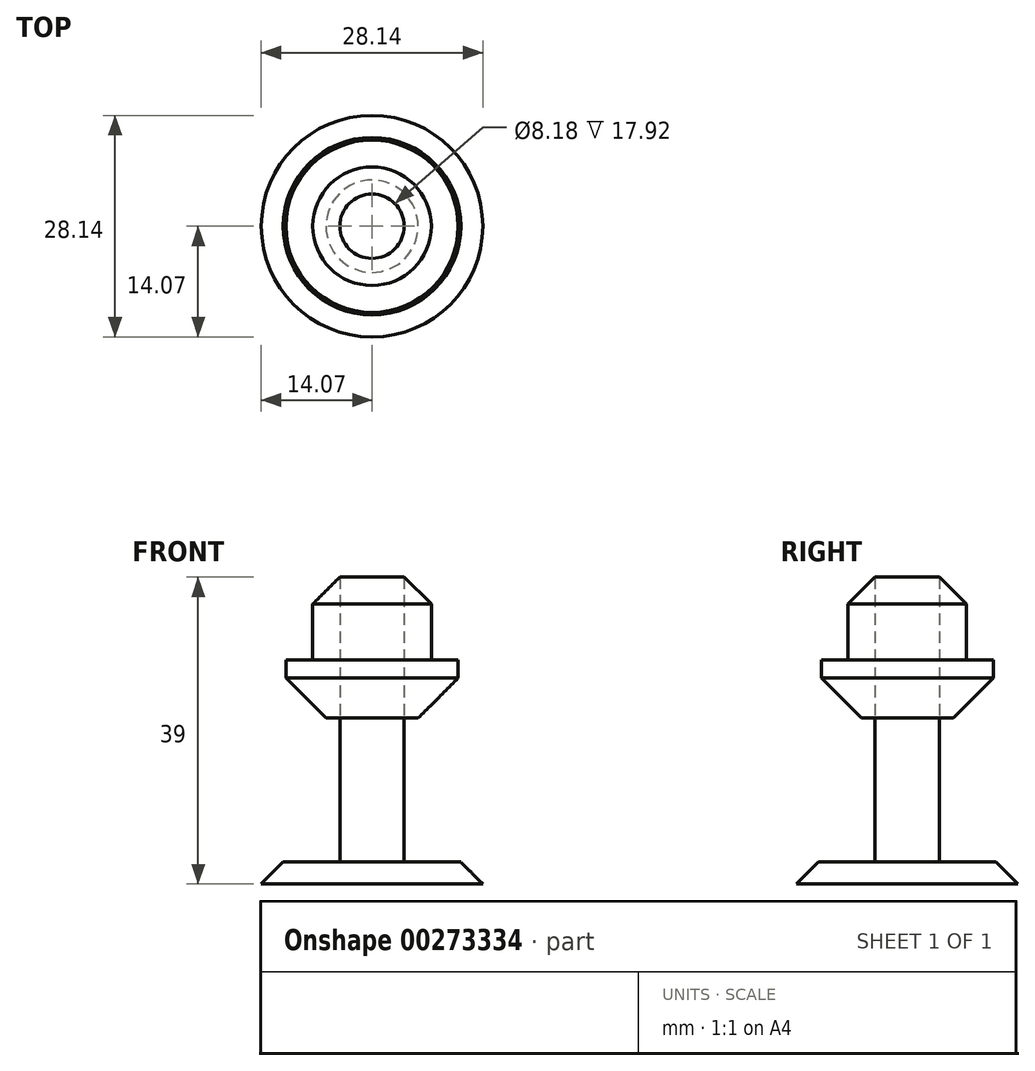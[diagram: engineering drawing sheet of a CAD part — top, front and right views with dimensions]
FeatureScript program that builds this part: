
annotation { "Feature Type Name" : "Feature", "Feature Type Description" : "" }
export const myFeature = defineFeature(function(context is Context, id is Id, definition is map)
    precondition{}
    {
        {
            var Q0;
            Q0=qCreatedBy(makeId("Top.planeOp"),FACE);
            var sketch = newSketch(context, id + "F0", { "sketchPlane" : qUnion([Q0])});
            skCircle(sketch, "E0", {"center": v(0, 0) * mm, "radius": 16.35 * mm});
            skSolve(sketch);
        }
        {
            var Q0;
            Q0=makeQuery(id+"F0.imprint","IMPRINT",FACE,{"disambiguationData":[TD([[makeQuery(id+"F0.imprint","IMPRINT",EDGE,{"derivedFrom":sQuery(id+"F0.wireOp",EDGE,"E0")}),1.0]])]});
            extrude(context, id + "F1", {"entities" : qUnion([Q0]), "depth" : 2.8 * mm});
        }
        {
            var Q0;
            Q0=makeQuery(id+"F1.opExtrude","CAP_EDGE",EDGE,{"disambiguationData":[OSD([sQuery(id+"F0.wireOp",EDGE,"E0")])],"isStart":false});
            chamfer(context, id + "F2", {"entities" : qUnion([Q0]), "width" : 5.08 * mm, "tangentPropagation" : true});
        }
        {
            var Q0;
            Q0=makeQuery(id+"F1.opExtrude","CAP_FACE",FACE,{"disambiguationData":[OSD([sQuery(id+"F0.wireOp",EDGE,"E0")])],"isStart":false});
            var sketch = newSketch(context, id + "F3", { "sketchPlane" : qUnion([Q0])});
            skCircle(sketch, "E1", {"center": v(0, 0) * mm, "radius": 5.59 * mm});
            skSolve(sketch);
        }
        {
            var Q0;
            Q0=sQuery(id+"F3.wireOp",EDGE,"E1");
            extrude(context, id + "F4", {"bodyType" : ToolBodyType.SURFACE, "surfaceEntities" : qUnion([Q0]), "depth" : 9.65 * mm});
        }
        {
            var Q0;
            Q0=makeQuery(id+"F1.opExtrude","CAP_FACE",FACE,{"disambiguationData":[OSD([sQuery(id+"F0.wireOp",EDGE,"E0")])],"isStart":false});
            var sketch = newSketch(context, id + "F5", { "sketchPlane" : qUnion([Q0])});
            skCircle(sketch, "E2", {"center": v(0, 0) * mm, "radius": 4.1 * mm});
            skSolve(sketch);
        }
        {
            var Q0;
            Q0=makeQuery(id+"F5.imprint","IMPRINT",FACE,{"disambiguationData":[TD([[makeQuery(id+"F5.imprint","IMPRINT",EDGE,{"derivedFrom":sQuery(id+"F5.wireOp",EDGE,"E2")}),1.0]])]});
            extrude(context, id + "F6", {"entities" : qUnion([Q0]), "operationType" : NewBodyOperationType.ADD, "depth" : 18.29 * mm});
        }
        {
            var Q0;
            Q0=makeQuery(id+"F6.opExtrude","CAP_FACE",FACE,{"disambiguationData":[OSD([sQuery(id+"F5.wireOp",EDGE,"E2")])],"isStart":false});
            var sketch = newSketch(context, id + "F7", { "sketchPlane" : qUnion([Q0])});
            skCircle(sketch, "E3", {"center": v(0, 0) * mm, "radius": 7.53 * mm});
            skSolve(sketch);
        }
        {
            var Q0;
            Q0=makeQuery(id+"F7.imprint","IMPRINT",FACE,{"disambiguationData":[TD([[makeQuery(id+"F7.imprint","IMPRINT",EDGE,{"derivedFrom":sQuery(id+"F7.wireOp",EDGE,"E3")}),1.0]])]});
            extrude(context, id + "F8", {"entities" : qUnion([Q0]), "depth" : 19.56 * mm});
        }
        {
            var Q0;
            Q0=makeQuery(id+"F8.opExtrude","CAP_EDGE",EDGE,{"disambiguationData":[OSD([sQuery(id+"F7.wireOp",EDGE,"E3")])],"isStart":false});
            var Q1;
            Q1=makeQuery(id+"F4.opExtrude","SWEPT_FACE",FACE,{"disambiguationData":[OSD([sQuery(id+"F3.wireOp",EDGE,"E1")])]});
            chamfer(context, id + "F9", {"entities" : qUnion([Q0, Q1]), "width" : 5.08 * mm, "tangentPropagation" : true});
        }
        {
            var Q0;
            Q0=makeQuery(id+"F6.opExtrude","CAP_FACE",FACE,{"disambiguationData":[OSD([sQuery(id+"F5.wireOp",EDGE,"E2")])],"isStart":false});
            var sketch = newSketch(context, id + "F10", { "sketchPlane" : qUnion([Q0])});
            skCircle(sketch, "E4", {"center": v(0, 0) * mm, "radius": 10.94 * mm});
            skSolve(sketch);
        }
        {
            var Q0;
            Q0=makeQuery(id+"F10.imprint","IMPRINT",FACE,{"disambiguationData":[TD([[makeQuery(id+"F10.imprint","IMPRINT",EDGE,{"derivedFrom":sQuery(id+"F10.wireOp",EDGE,"E4")}),1.0]])]});
            extrude(context, id + "F11", {"entities" : qUnion([Q0]), "operationType" : NewBodyOperationType.ADD, "depth" : 7.37 * mm});
        }
        {
            var Q0;
            Q0=makeQuery(id+"F11.opExtrude","CAP_EDGE",EDGE,{"disambiguationData":[OSD([sQuery(id+"F10.wireOp",EDGE,"E4")])],"isStart":true});
            chamfer(context, id + "F12", {"entities" : qUnion([Q0]), "width" : 5.08 * mm, "tangentPropagation" : true});
        }
    });
